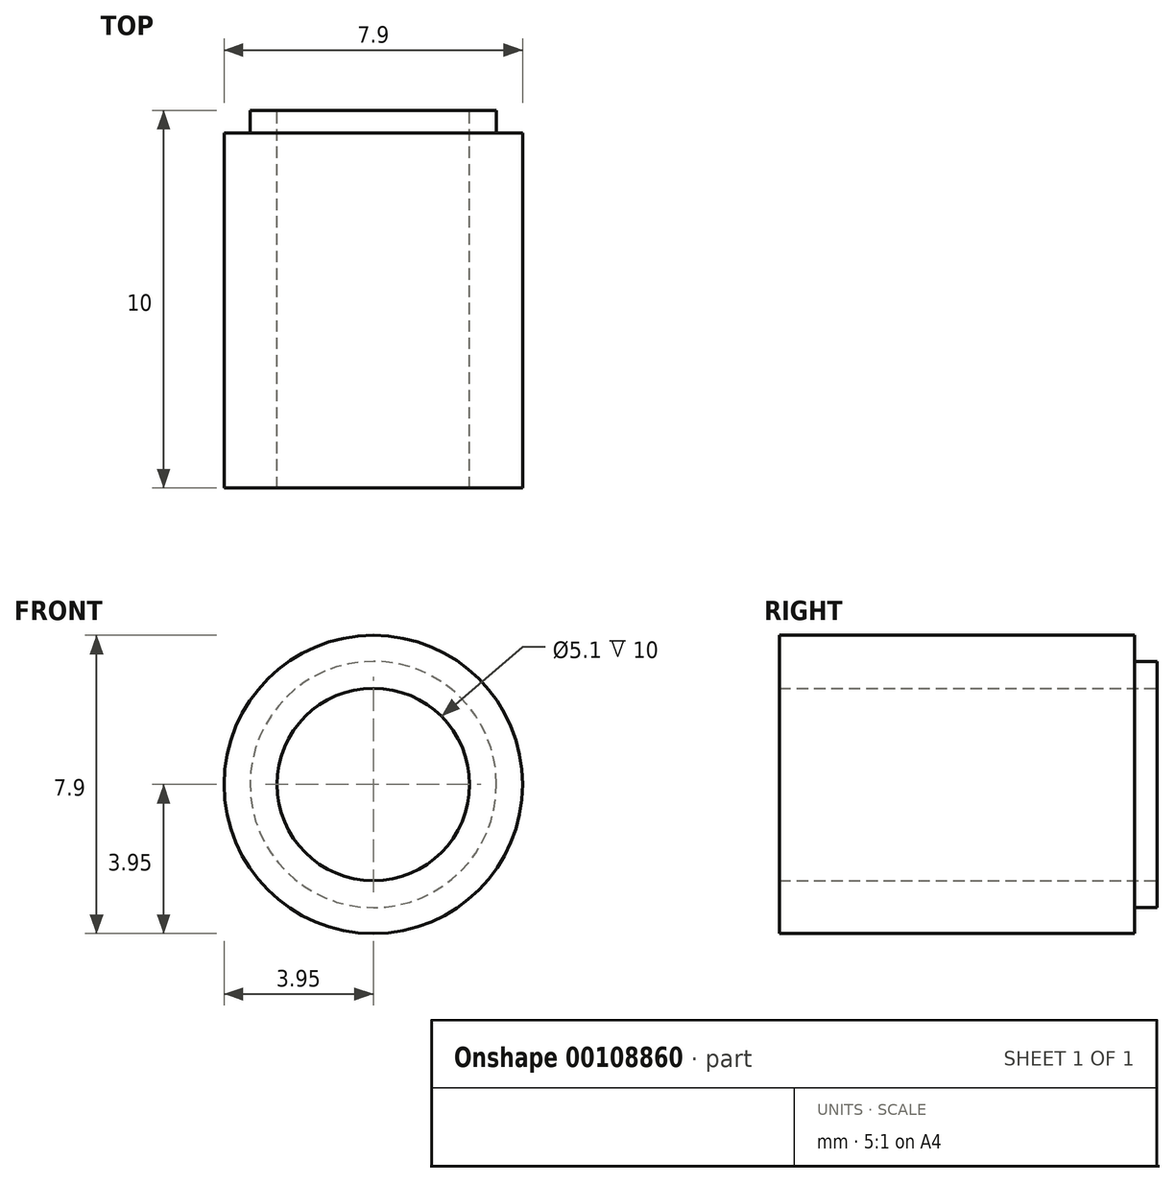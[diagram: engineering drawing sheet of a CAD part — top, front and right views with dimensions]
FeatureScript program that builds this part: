
annotation { "Feature Type Name" : "Feature", "Feature Type Description" : "" }
export const myFeature = defineFeature(function(context is Context, id is Id, definition is map)
    precondition{}
    {
        {
            var Q0;
            Q0=qCreatedBy(makeId("Front.planeOp"),FACE);
            var sketch = newSketch(context, id + "F0", { "sketchPlane" : qUnion([Q0])});
            skCircle(sketch, "E0", {"center": v(0, 0) * mm, "radius": 3.95 * mm});
            skCircle(sketch, "E1", {"center": v(0, 0) * mm, "radius": 2.55 * mm});
            skCircle(sketch, "E2", {"center": v(0, 0) * mm, "radius": 3.26 * mm});
            skSolve(sketch);
        }
        {
            var Q0;
            Q0=makeQuery(id+"F0.imprint","IMPRINT",FACE,{"disambiguationData":[TD([[makeQuery(id+"F0.imprint","IMPRINT",EDGE,{"derivedFrom":sQuery(id+"F0.wireOp",EDGE,"E0")}),1.0]])]});
            var Q1;
            Q1=makeQuery(id+"F0.imprint","IMPRINT",FACE,{"disambiguationData":[TD([[makeQuery(id+"F0.imprint","IMPRINT",EDGE,{"derivedFrom":sQuery(id+"F0.wireOp",EDGE,"E1")}),-1.0]])]});
            extrude(context, id + "F1", {"entities" : qUnion([Q0, Q1]), "depth" : 10 * mm});
        }
        {
            var Q0;
            Q0=makeQuery(id+"F0.imprint","IMPRINT",FACE,{"disambiguationData":[TD([[makeQuery(id+"F0.imprint","IMPRINT",EDGE,{"derivedFrom":sQuery(id+"F0.wireOp",EDGE,"E0")}),1.0]])]});
            extrude(context, id + "F2", {"entities" : qUnion([Q0]), "operationType" : NewBodyOperationType.REMOVE, "depth" : 0.6 * mm});
        }
    });
